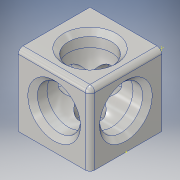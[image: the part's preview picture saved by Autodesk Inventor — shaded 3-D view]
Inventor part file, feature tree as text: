
AUTODESK INVENTOR PART (.ipt)
format: ipt  version: 2016 (Build 200138000, 138)  size: 359,936 bytes
history: native  units: in
note: dims shown in document units (in); Inventor stores cm internally (conversion verified against a paired STEP export)
features: sketch x10, extrude x7, other x6, loft x3, chamfer x3, fillet x1
ambient origin geometry x8: Origin, YZ Plane, XZ Plane, XY Plane, X Axis, Y Axis, Z Axis, Center Point
bodies: Solid1 (feature_tree)
feature tree (30):
  extrude  "Extrusion1"  Depth=1.1811in
  sketch  "Sketch2"  dims[d4=0.7087in d5=0.3543in]
  sketch  "Sketch3"  dims[d6=0.0787in d7=0.7087in]
  fillet  "Fillet1"  Radius=1.1811in
  sketch  "Sketch4"  dims[d8=0.3543in d9=0.2362in d10=0.0in]
  sketch  "Sketch5"  dims[d12=0.5906in d13=0.5906in]
  extrude  "Extrusion2"  Depth=0.3543in
  sketch  "Sketch6"  dims[d14=0.7087in d15=0.3543in]
  sketch  "Sketch7"  dims[d16=0.2362in d17=0.0in d18=0.2362in d19=0.0in]
  sketch  "Sketch8"  dims[d20=0.1181in d21=0.0in d22=0.3937in d23=90.0deg d24=0.3937in d25=90.0deg]
  sketch  "Sketch9"  dims[d26=0.1181in d27=0.0in d28=0.1181in d29=0.0in]
  sketch  "Sketch10"  dims[d30=0.3937in d31=90.0deg d32=0.3937in d33=90.0deg d34=0.3937in d35=90.0deg d36=0.3937in d37=90.0deg d38=0.0787in d39=0.0787in d40=45.0deg d41=0.0787in d42=0.0787in d43=45.0deg d44=0.0787in d45=0.0787in d46=45.0deg]
  extrude  "Extrusion3"  Depth=0.7087in
  extrude  "Extrusion4"  Depth=0.3543in TaperAngle=0.0deg
  extrude  "Extrusion5"  Depth=0.5906in
  loft  "Loft1"
  extrude  "Extrusion6"  Depth=0.2362in TaperAngle=0.0deg
  extrude  "Extrusion7"  Depth=0.3937in TaperAngle=90.0deg
  loft  "Loft2"
  loft  "Loft3"
  chamfer  "Chamfer1"  Distance=0.0787in Angle=45.0deg
  chamfer  "Chamfer2"  [1 undecoded]
  chamfer  "Chamfer3"  [1 undecoded]
  sketch  "Sketch1"  dims[d0=1.1811in d1=1.1811in d2=1.1811in d3=0.0in]
  other  "Edges1"
  other  "Edges2"
  other  "Edges3"
  other  "Edges4"
  other  "Edges5"
  other  "Edges6"
note: 2 required parameter values undecoded (feature->parameter linkage not recoverable at this tier; creation-order binding heuristic only, values carry confidence <= 0.55)
